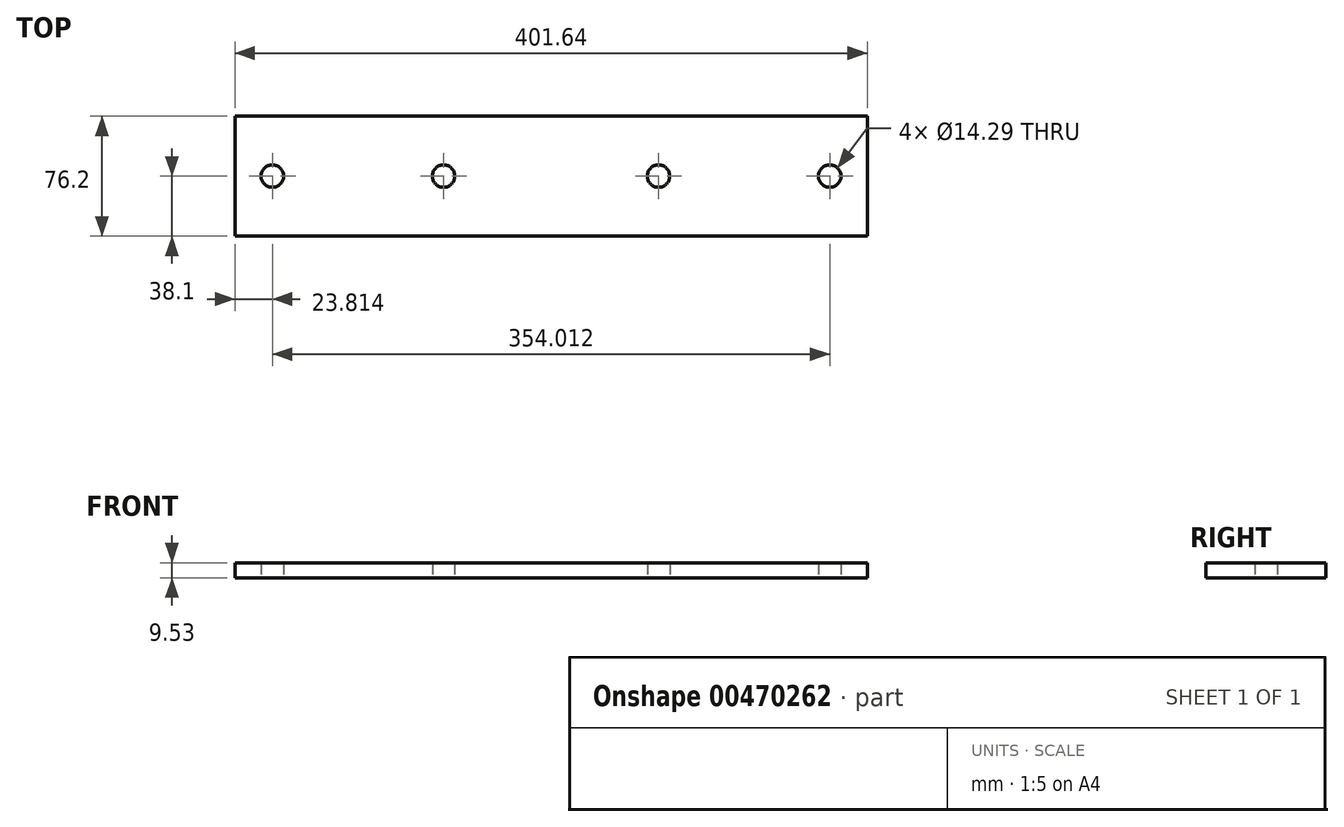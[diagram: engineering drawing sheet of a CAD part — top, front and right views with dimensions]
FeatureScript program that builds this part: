
annotation { "Feature Type Name" : "Feature", "Feature Type Description" : "" }
export const myFeature = defineFeature(function(context is Context, id is Id, definition is map)
    precondition{}
    {
        {
            var Q0;
            Q0=qCreatedBy(makeId("Top.planeOp"),FACE);
            var sketch = newSketch(context, id + "F0", { "sketchPlane" : qUnion([Q0])});
            skLineSegment(sketch, "E0.bottom", {"start": v(200.82, -38.1) * mm, "end": v(-200.82, -38.1) * mm});
            skLineSegment(sketch, "E0.top", {"start": v(200.82, 38.1) * mm, "end": v(-200.82, 38.1) * mm});
            skLineSegment(sketch, "E0.left", {"start": v(200.82, -38.1) * mm, "end": v(200.82, 38.1) * mm});
            skLineSegment(sketch, "E0.right", {"start": v(-200.82, -38.1) * mm, "end": v(-200.82, 38.1) * mm});
            skPoint(sketch, "E0.middle", {"position": v(0, 0) * mm});
            skCircle(sketch, "E1", {"center": v(-68.26, 0) * mm, "radius": 7.14 * mm});
            skCircle(sketch, "E2", {"center": v(-177, 0) * mm, "radius": 7.14 * mm});
            skPoint(sketch, "E2.centerSnap0", {"position": v(-200.82, 0) * mm});
            skCircle(sketch, "E3.MirrorC", {"center": v(68.26, 0) * mm, "radius": 7.14 * mm});
            skCircle(sketch, "E4.MirrorC", {"center": v(177, 0) * mm, "radius": 7.14 * mm});
            skSolve(sketch);
        }
        {
            var Q0;
            Q0=qSketchRegion(id+"F0",true);
            extrude(context, id + "F1", {"entities" : qUnion([Q0]), "depth" : 9.52 * mm});
        }
    });
